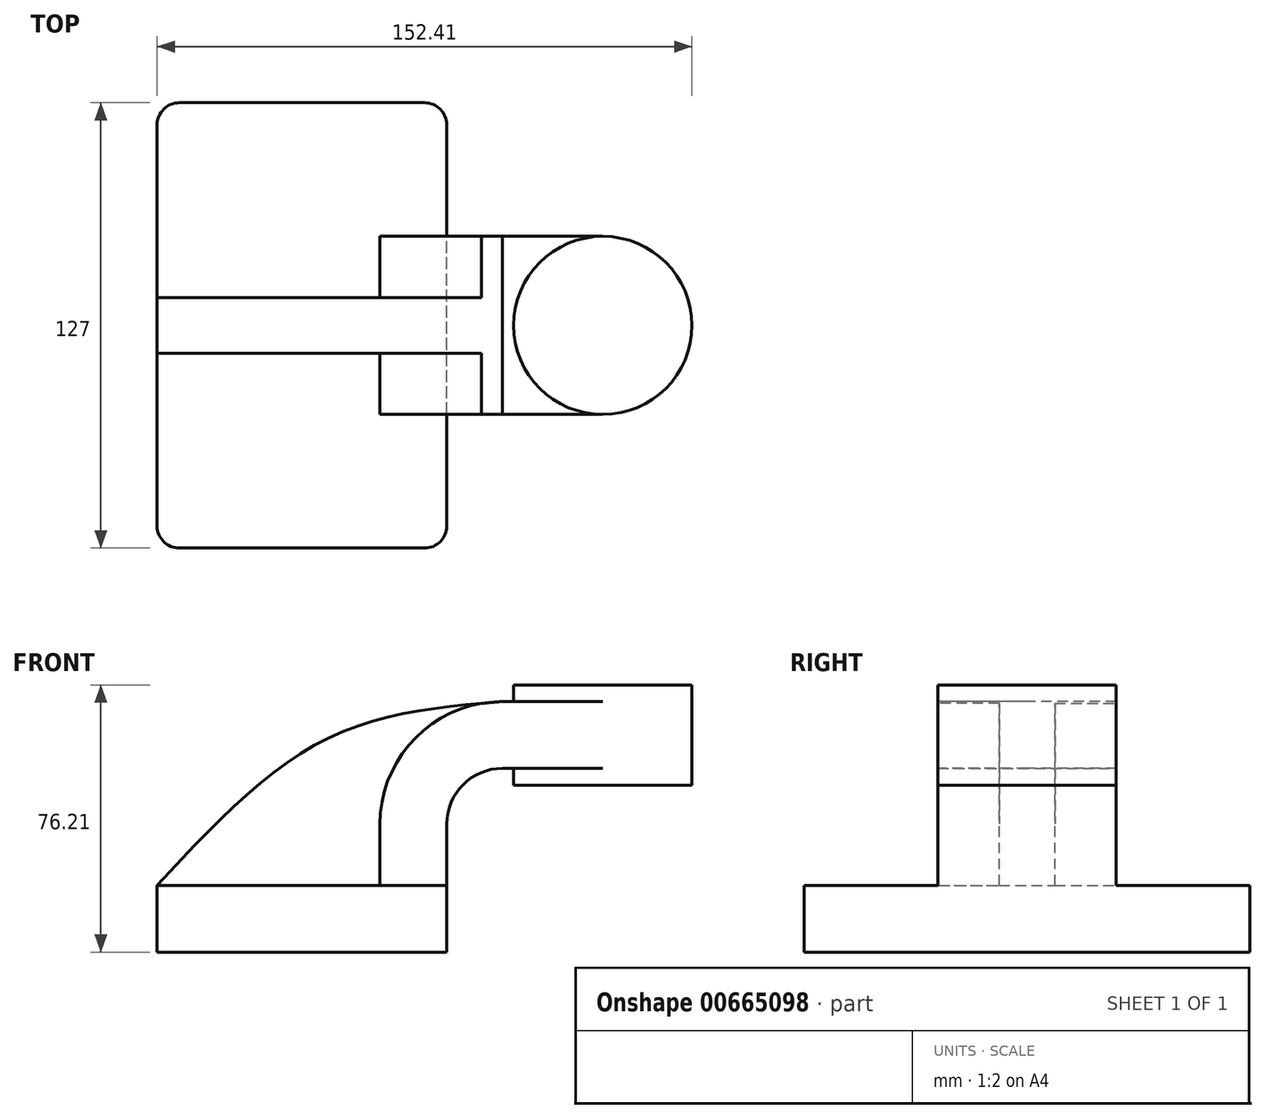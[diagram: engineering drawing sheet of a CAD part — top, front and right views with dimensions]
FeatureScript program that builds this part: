
annotation { "Feature Type Name" : "Feature", "Feature Type Description" : "" }
export const myFeature = defineFeature(function(context is Context, id is Id, definition is map)
    precondition{}
    {
        {
            var Q0;
            Q0=qCreatedBy(makeId("Front.planeOp"),FACE);
            var sketch = newSketch(context, id + "F0", { "sketchPlane" : qUnion([Q0])});
            skLineSegment(sketch, "E0.bottom", {"start": v(41.28, -9.52) * mm, "end": v(-41.28, -9.53) * mm});
            skLineSegment(sketch, "E0.top", {"start": v(41.28, 9.53) * mm, "end": v(-41.28, 9.53) * mm});
            skLineSegment(sketch, "E0.left", {"start": v(41.28, -9.52) * mm, "end": v(41.28, 9.53) * mm});
            skLineSegment(sketch, "E0.right", {"start": v(-41.28, -9.53) * mm, "end": v(-41.28, 9.53) * mm});
            skPoint(sketch, "E0.middle", {"position": v(0, 0) * mm});
            skLineSegment(sketch, "E1.bottom", {"start": v(111.13, 38.1) * mm, "end": v(60.32, 38.1) * mm});
            skLineSegment(sketch, "E1.top", {"start": v(111.13, 66.68) * mm, "end": v(60.32, 66.68) * mm});
            skLineSegment(sketch, "E1.left", {"start": v(111.12, 38.1) * mm, "end": v(111.12, 66.68) * mm});
            skLineSegment(sketch, "E1.right", {"start": v(60.32, 38.1) * mm, "end": v(60.32, 66.68) * mm});
            skPoint(sketch, "E1.middle", {"position": v(85.73, 52.39) * mm});
            skLineSegment(sketch, "E2", {"start": v(41.28, 9.53) * mm, "end": v(41.28, 27) * mm});
            skArc(sketch, "E3", {"start": v(41.27, 27) * mm, "mid": v(45.92, 38.23) * mm, "end": v(57.15, 42.88) * mm});
            skLineSegment(sketch, "E4", {"start": v(57.15, 42.88) * mm, "end": v(85.73, 42.88) * mm});
            skPoint(sketch, "E4.endSnap0", {"position": v(85.73, 38.1) * mm});
            skLineSegment(sketch, "E5.0", {"start": v(57.15, 61.93) * mm, "end": v(85.73, 61.93) * mm});
            skArc(sketch, "E5.1", {"start": v(22.23, 27) * mm, "mid": v(32.45, 51.7) * mm, "end": v(57.15, 61.93) * mm});
            skLineSegment(sketch, "E5.2", {"start": v(22.22, 9.53) * mm, "end": v(22.22, 27) * mm});
            skLineSegment(sketch, "E6", {"start": v(85.73, 38.1) * mm, "end": v(85.73, 66.68) * mm});
            skFitSpline(sketch, "E7", {"points": [v(-41.28, 9.52) * mm, v(6.82, 51.18) * mm, v(57.15, 61.93) * mm], "startDerivative": vector(87.42, 93.96) * mm, "endDerivative": vector(109.82, 9.34) * mm});
            skSolve(sketch);
        }
        {
            var Q0;
            Q0=makeQuery(id+"F0.imprint","IMPRINT",FACE,{"disambiguationData":[TD([[makeQuery(id+"F0.imprint","IMPRINT",EDGE,{"derivedFrom":sQuery(id+"F0.wireOp",EDGE,"E0.bottom")}),-1.0]])]});
            extrude(context, id + "F1", {"entities" : qUnion([Q0]), "endBound" : BoundingType.SYMMETRIC, "depth" : 127 * mm, "offsetDistance" : 25.4 * mm});
        }
        {
            var Q0;
            {var subQ1=sQuery(id+"F0.wireOp",EDGE,"E2");Q0=makeQuery(id+"F0.imprint","IMPRINT",FACE,{"disambiguationData":[TD([[makeQuery(id+"F0.imprint","IMPRINT",EDGE,{"derivedFrom":subQ1}),1.0]])]});}
            var Q1;
            {var subQ0=sQuery(id+"F0.wireOp",EDGE,"E4");var subQ1=sQuery(id+"F0.wireOp",EDGE,"E1.right");var subQ2=makeQuery(id+"F0.imprint","INTERSECT",VERTEX,{"derivedFrom":[subQ1,subQ0]});Q1=makeQuery(id+"F0.imprint","IMPRINT",FACE,{"disambiguationData":[TD([[makeQuery(id+"F0.imprint","IMPRINT",EDGE,{"disambiguationData":[TD([[subQ2,-1.0]])],"derivedFrom":subQ1}),-1.0]])]});}
            extrude(context, id + "F2", {"entities" : qUnion([Q0, Q1]), "operationType" : NewBodyOperationType.ADD, "endBound" : BoundingType.SYMMETRIC, "depth" : 50.8 * mm, "offsetDistance" : 25.4 * mm});
        }
        {
            var Q0;
            {var subQ3=sQuery(id+"F0.wireOp",EDGE,"E5.2");Q0=makeQuery(id+"F0.imprint","IMPRINT",FACE,{"disambiguationData":[TD([[makeQuery(id+"F0.imprint","IMPRINT",EDGE,{"derivedFrom":subQ3}),1.0]])]});}
            extrude(context, id + "F3", {"entities" : qUnion([Q0]), "operationType" : NewBodyOperationType.ADD, "endBound" : BoundingType.SYMMETRIC, "depth" : 15.88 * mm, "offsetDistance" : 25.4 * mm});
        }
        {
            var Q0;
            {var subQ0=sQuery(id+"F0.wireOp",EDGE,"E1.left");Q0=makeQuery(id+"F0.imprint","IMPRINT",FACE,{"disambiguationData":[TD([[makeQuery(id+"F0.imprint","IMPRINT",EDGE,{"derivedFrom":subQ0}),1.0]])]});}
            var Q1;
            Q1=sQuery(id+"F0.wireOp",EDGE,"E6");
            revolve(context, id + "F4", {"operationType" : NewBodyOperationType.ADD, "entities" : qUnion([Q0]), "axis" : qUnion([Q1]), "revolveType" : RevolveType.FULL});
        }
        {
            var Q0;
            Q0=makeQuery(id+"F1.opExtrude","CAP_EDGE",EDGE,{"disambiguationData":[OSD([sQuery(id+"F0.wireOp",EDGE,"E0.left")])],"isStart":false});
            var Q1;
            Q1=makeQuery(id+"F1.opExtrude","CAP_EDGE",EDGE,{"disambiguationData":[OSD([sQuery(id+"F0.wireOp",EDGE,"E0.right")])],"isStart":false});
            var Q2;
            Q2=makeQuery(id+"F1.opExtrude","CAP_EDGE",EDGE,{"disambiguationData":[OSD([sQuery(id+"F0.wireOp",EDGE,"E0.left")])],"isStart":true});
            var Q3;
            Q3=makeQuery(id+"F1.opExtrude","CAP_EDGE",EDGE,{"disambiguationData":[OSD([sQuery(id+"F0.wireOp",EDGE,"E0.right")])],"isStart":true});
            fillet(context, id + "F5", {"entities" : qUnion([Q0, Q1, Q2, Q3]), "radius" : 6.35 * mm, "tangentPropagation" : true, "allowEdgeOverflow" : false});
        }
    });
